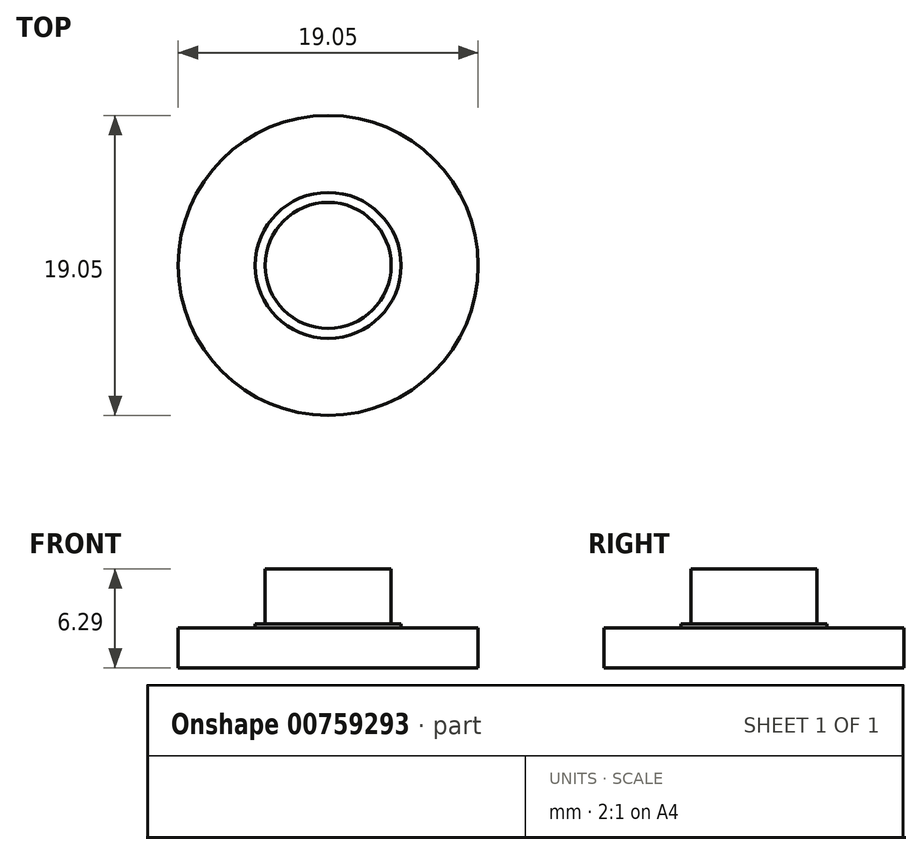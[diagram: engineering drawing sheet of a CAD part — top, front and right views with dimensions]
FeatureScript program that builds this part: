
annotation { "Feature Type Name" : "Feature", "Feature Type Description" : "" }
export const myFeature = defineFeature(function(context is Context, id is Id, definition is map)
    precondition{}
    {
        {
            var Q0;
            Q0=qCreatedBy(makeId("Top.planeOp"),FACE);
            var sketch = newSketch(context, id + "F0", { "sketchPlane" : qUnion([Q0])});
            skCircle(sketch, "E0", {"center": v(-69.42, 31.22) * mm, "radius": 4 * mm});
            skCircle(sketch, "E1", {"center": v(-69.42, 31.22) * mm, "radius": 9.53 * mm});
            skCircle(sketch, "E2", {"center": v(-69.42, 31.22) * mm, "radius": 4.63 * mm});
            skSolve(sketch);
        }
        {
            var Q0;
            Q0=makeQuery(id+"F0.imprint","IMPRINT",FACE,{"disambiguationData":[TD([[makeQuery(id+"F0.imprint","IMPRINT",EDGE,{"derivedFrom":sQuery(id+"F0.wireOp",EDGE,"E1")}),1.0]])]});
            extrude(context, id + "F1", {"entities" : qUnion([Q0]), "depth" : 2.54 * mm, "offsetDistance" : 25.4 * mm});
        }
        {
            var Q0;
            Q0=makeQuery(id+"F0.imprint","IMPRINT",FACE,{"disambiguationData":[TD([[makeQuery(id+"F0.imprint","IMPRINT",EDGE,{"derivedFrom":sQuery(id+"F0.wireOp",EDGE,"E0")}),-1.0]])]});
            extrude(context, id + "F2", {"entities" : qUnion([Q0]), "operationType" : NewBodyOperationType.ADD, "depth" : 2.8 * mm, "offsetDistance" : 25.4 * mm});
        }
        {
            var Q0;
            Q0=makeQuery(id+"F0.imprint","IMPRINT",FACE,{"disambiguationData":[TD([[makeQuery(id+"F0.imprint","IMPRINT",EDGE,{"derivedFrom":sQuery(id+"F0.wireOp",EDGE,"E0")}),1.0]])]});
            extrude(context, id + "F3", {"entities" : qUnion([Q0]), "operationType" : NewBodyOperationType.ADD, "depth" : 3.5 * mm + 2.8 * mm, "offsetDistance" : 25.4 * mm});
        }
    });
